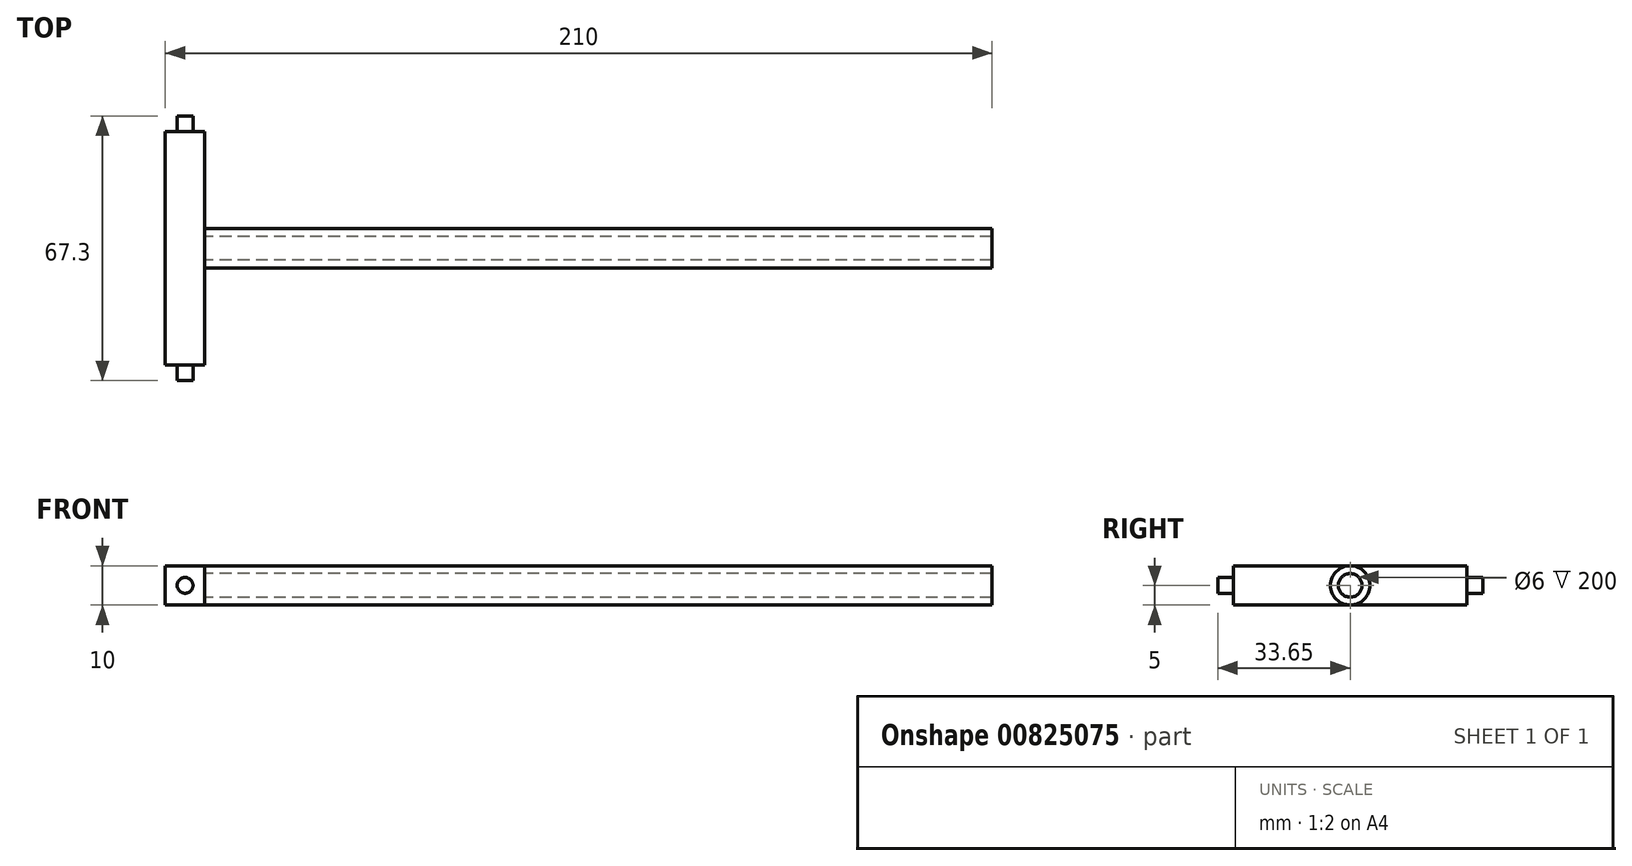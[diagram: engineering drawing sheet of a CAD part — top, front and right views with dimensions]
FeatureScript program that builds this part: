
annotation { "Feature Type Name" : "Feature", "Feature Type Description" : "" }
export const myFeature = defineFeature(function(context is Context, id is Id, definition is map)
    precondition{}
    {
        {
            var Q0;
            Q0=qCreatedBy(makeId("Front.planeOp"),FACE);
            var sketch = newSketch(context, id + "F0", { "sketchPlane" : qUnion([Q0])});
            skLineSegment(sketch, "E0.bottom", {"start": v(-5, 5) * mm, "end": v(5, 5) * mm});
            skLineSegment(sketch, "E0.top", {"start": v(-5, -5) * mm, "end": v(5, -5) * mm});
            skLineSegment(sketch, "E0.left", {"start": v(-5, 5) * mm, "end": v(-5, -5) * mm});
            skLineSegment(sketch, "E0.right", {"start": v(5, 5) * mm, "end": v(5, -5) * mm});
            skPoint(sketch, "E0.middle", {"position": v(0, 0) * mm});
            skSolve(sketch);
        }
        {
            var Q0;
            Q0=makeQuery(id+"F0.imprint","IMPRINT",FACE,{"disambiguationData":[TD([[makeQuery(id+"F0.imprint","IMPRINT",EDGE,{"derivedFrom":sQuery(id+"F0.wireOp",EDGE,"E0.bottom")}),-1.0]])]});
            extrude(context, id + "F1", {"entities" : qUnion([Q0]), "endBound" : BoundingType.SYMMETRIC, "depth" : 67.3 * mm, "offsetDistance" : 25 * mm});
        }
        {
            var Q0;
            Q0=makeQuery(id+"F1.opExtrude","CAP_FACE",FACE,{"disambiguationData":[OSD([sQuery(id+"F0.wireOp",EDGE,"E0.bottom"),sQuery(id+"F0.wireOp",EDGE,"E0.top"),sQuery(id+"F0.wireOp",EDGE,"E0.left"),sQuery(id+"F0.wireOp",EDGE,"E0.right")])],"isStart":false});
            var sketch = newSketch(context, id + "F2", { "sketchPlane" : qUnion([Q0])});
            skCircle(sketch, "E1", {"center": v(0, 0) * mm, "radius": 2 * mm});
            skSolve(sketch);
        }
        {
            var Q0;
            Q0=makeQuery(id+"F2.imprint","IMPRINT",FACE,{"disambiguationData":[TD([[makeQuery(id+"F2.imprint","IMPRINT",EDGE,{"derivedFrom":sQuery(id+"F2.wireOp",EDGE,"E1")}),-1.0]])]});
            extrude(context, id + "F3", {"entities" : qUnion([Q0]), "operationType" : NewBodyOperationType.REMOVE, "oppositeDirection" : true, "depth" : 4 * mm, "offsetDistance" : 25 * mm});
        }
        {
            var Q0;
            Q0=makeQuery(id+"F1.opExtrude","CAP_FACE",FACE,{"disambiguationData":[OSD([sQuery(id+"F0.wireOp",EDGE,"E0.bottom"),sQuery(id+"F0.wireOp",EDGE,"E0.top"),sQuery(id+"F0.wireOp",EDGE,"E0.left"),sQuery(id+"F0.wireOp",EDGE,"E0.right")])],"isStart":true});
            var sketch = newSketch(context, id + "F4", { "sketchPlane" : qUnion([Q0])});
            skCircle(sketch, "E2", {"center": v(0, 0) * mm, "radius": 2 * mm});
            skSolve(sketch);
        }
        {
            var Q0;
            Q0=makeQuery(id+"F4.imprint","IMPRINT",FACE,{"disambiguationData":[TD([[makeQuery(id+"F4.imprint","IMPRINT",EDGE,{"derivedFrom":sQuery(id+"F4.wireOp",EDGE,"E2")}),-1.0]])]});
            extrude(context, id + "F5", {"entities" : qUnion([Q0]), "operationType" : NewBodyOperationType.REMOVE, "oppositeDirection" : true, "depth" : 4 * mm, "offsetDistance" : 25 * mm});
        }
        {
            var Q0;
            Q0=makeQuery(id+"F1.opExtrude","SWEPT_FACE",FACE,{"disambiguationData":[OSD([sQuery(id+"F0.wireOp",EDGE,"E0.right")])]});
            var sketch = newSketch(context, id + "F6", { "sketchPlane" : qUnion([Q0])});
            skCircle(sketch, "E3", {"center": v(0, 0) * mm, "radius": 5 * mm});
            skCircle(sketch, "E4", {"center": v(0, 0) * mm, "radius": 3 * mm});
            skSolve(sketch);
        }
        {
            var Q0;
            Q0=makeQuery(id+"F6.imprint","IMPRINT",FACE,{"disambiguationData":[TD([[makeQuery(id+"F6.imprint","IMPRINT",EDGE,{"derivedFrom":sQuery(id+"F6.wireOp",EDGE,"E4")}),-1.0]])]});
            extrude(context, id + "F7", {"entities" : qUnion([Q0]), "operationType" : NewBodyOperationType.ADD, "depth" : 200 * mm, "offsetDistance" : 25 * mm});
        }
    });
